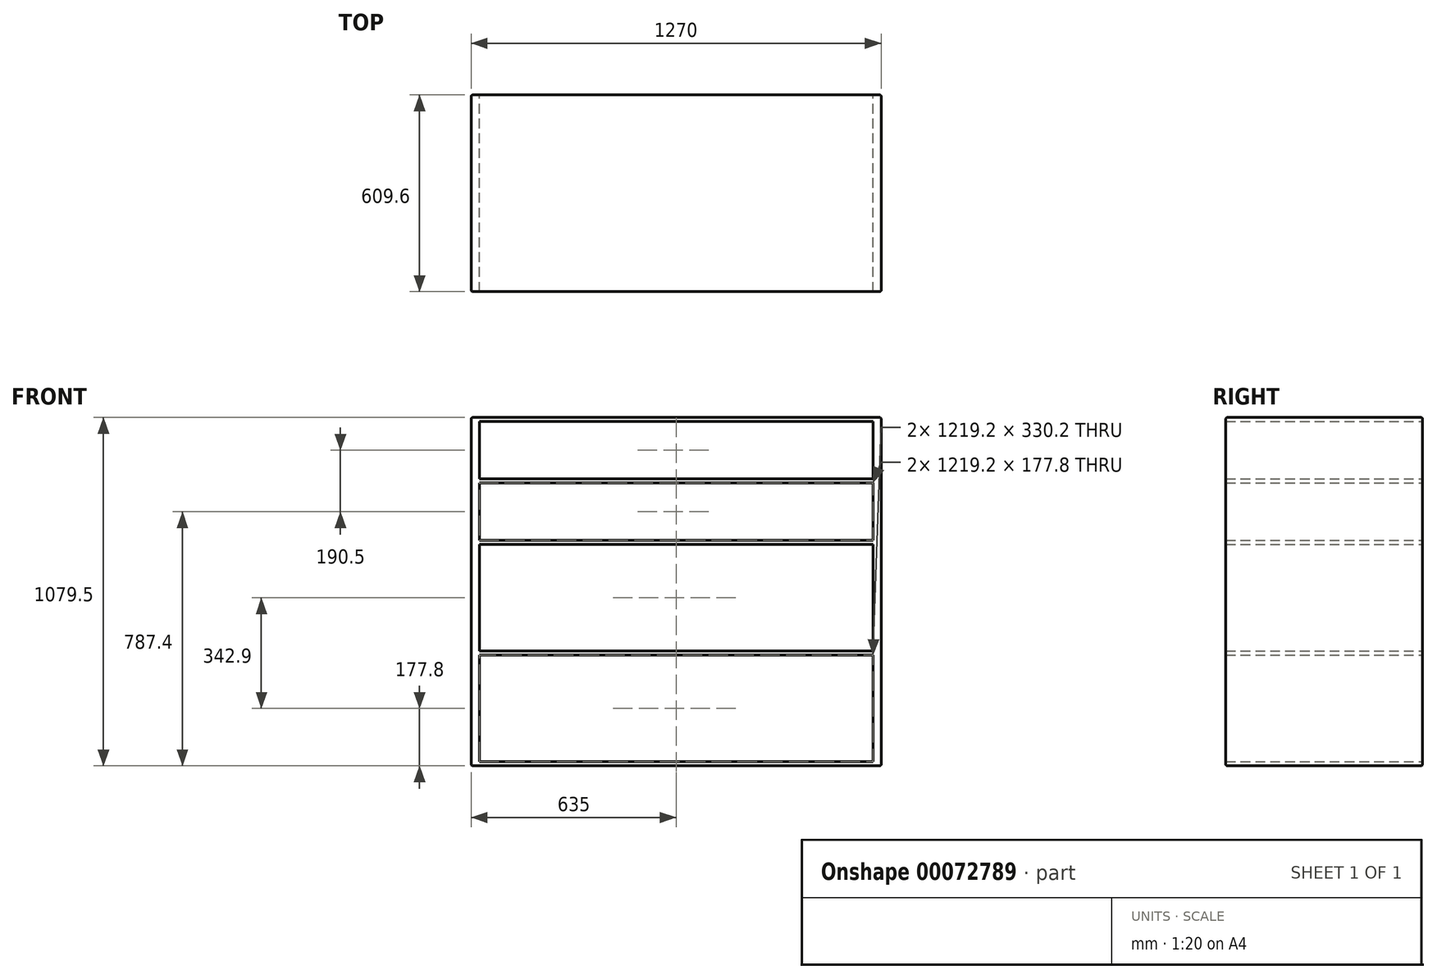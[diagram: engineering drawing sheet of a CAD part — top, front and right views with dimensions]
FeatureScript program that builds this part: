
annotation { "Feature Type Name" : "Feature", "Feature Type Description" : "" }
export const myFeature = defineFeature(function(context is Context, id is Id, definition is map)
    precondition{}
    {
        {
            var Q0;
            Q0=qCreatedBy(makeId("Right.planeOp"),FACE);
            var sketch = newSketch(context, id + "F0", { "sketchPlane" : qUnion([Q0])});
            skLineSegment(sketch, "E0.bottom", {"start": v(0, 0) * mm, "end": v(609.6, 0) * mm});
            skLineSegment(sketch, "E0.top", {"start": v(0, 1079.5) * mm, "end": v(609.6, 1079.5) * mm});
            skLineSegment(sketch, "E0.left", {"start": v(0, 0) * mm, "end": v(0, 1079.5) * mm});
            skLineSegment(sketch, "E0.right", {"start": v(609.6, 0) * mm, "end": v(609.6, 1079.5) * mm});
            skSolve(sketch);
        }
        {
            var Q0;
            Q0=makeQuery(id+"F0.imprint","IMPRINT",FACE,{"disambiguationData":[TD([[makeQuery(id+"F0.imprint","IMPRINT",EDGE,{"derivedFrom":sQuery(id+"F0.wireOp",EDGE,"E0.bottom")}),1.0]])]});
            extrude(context, id + "F1", {"entities" : qUnion([Q0]), "depth" : 25.4 * mm});
        }
        {
            var Q0;
            Q0=makeQuery(id+"F1.opExtrude","CAP_FACE",FACE,{"disambiguationData":[OSD([sQuery(id+"F0.wireOp",EDGE,"E0.bottom"),sQuery(id+"F0.wireOp",EDGE,"E0.top"),sQuery(id+"F0.wireOp",EDGE,"E0.left"),sQuery(id+"F0.wireOp",EDGE,"E0.right")])],"isStart":false});
            var sketch = newSketch(context, id + "F2", { "sketchPlane" : qUnion([Q0])});
            skLineSegment(sketch, "E1.bottom", {"start": v(0, 0) * mm, "end": v(609.6, 0) * mm});
            skLineSegment(sketch, "E1.top", {"start": v(0, 12.7) * mm, "end": v(609.6, 12.7) * mm});
            skLineSegment(sketch, "E1.left", {"start": v(0, 0) * mm, "end": v(0, 12.7) * mm});
            skLineSegment(sketch, "E1.right", {"start": v(609.6, 0) * mm, "end": v(609.6, 12.7) * mm});
            skSolve(sketch);
        }
        {
            var Q0;
            Q0=makeQuery(id+"F2.imprint","IMPRINT",FACE,{"disambiguationData":[TD([[makeQuery(id+"F2.imprint","IMPRINT",EDGE,{"derivedFrom":sQuery(id+"F2.wireOp",EDGE,"E1.bottom")}),1.0]])]});
            extrude(context, id + "F3", {"entities" : qUnion([Q0]), "operationType" : NewBodyOperationType.ADD, "depth" : 609.6 * mm});
        }
        {
            var Q0;
            Q0=makeQuery(id+"F1.opExtrude","CAP_FACE",FACE,{"disambiguationData":[OSD([sQuery(id+"F0.wireOp",EDGE,"E0.bottom"),sQuery(id+"F0.wireOp",EDGE,"E0.top"),sQuery(id+"F0.wireOp",EDGE,"E0.left"),sQuery(id+"F0.wireOp",EDGE,"E0.right")])],"isStart":false});
            var sketch = newSketch(context, id + "F4", { "sketchPlane" : qUnion([Q0])});
            skLineSegment(sketch, "E2", {"start": v(0, 12.7) * mm, "end": v(0, 342.9) * mm});
            skLineSegment(sketch, "E3.bottom", {"start": v(0, 342.9) * mm, "end": v(609.6, 342.9) * mm});
            skLineSegment(sketch, "E3.top", {"start": v(0, 355.6) * mm, "end": v(609.6, 355.6) * mm});
            skLineSegment(sketch, "E3.left", {"start": v(0, 342.9) * mm, "end": v(0, 355.6) * mm});
            skLineSegment(sketch, "E3.right", {"start": v(609.6, 342.9) * mm, "end": v(609.6, 355.6) * mm});
            skSolve(sketch);
        }
        {
            var Q0;
            Q0=makeQuery(id+"F4.imprint","IMPRINT",FACE,{"disambiguationData":[TD([[makeQuery(id+"F4.imprint","IMPRINT",EDGE,{"derivedFrom":sQuery(id+"F4.wireOp",EDGE,"E3.bottom")}),1.0]])]});
            extrude(context, id + "F5", {"entities" : qUnion([Q0]), "operationType" : NewBodyOperationType.ADD, "depth" : 609.6 * mm});
        }
        {
            var Q0;
            {var subQ0=sQuery(id+"F0.wireOp",EDGE,"E0.right");var subQ1=sQuery(id+"F0.wireOp",EDGE,"E0.left");var subQ2=sQuery(id+"F0.wireOp",EDGE,"E0.top");Q0=makeQuery(id+"F5.boolean.opBoolean","SPLIT",FACE,{"disambiguationData":[TD([makeQuery(id+"F1.opExtrude","SWEPT_FACE",FACE,{"disambiguationData":[OSD([subQ2])]})])],"derivedFrom":makeQuery(id+"F1.opExtrude","CAP_FACE",FACE,{"disambiguationData":[OSD([sQuery(id+"F0.wireOp",EDGE,"E0.bottom"),subQ2,subQ1,subQ0])],"isStart":false})});}
            var sketch = newSketch(context, id + "F6", { "sketchPlane" : qUnion([Q0])});
            skLineSegment(sketch, "E4", {"start": v(0, 355.6) * mm, "end": v(0, 685.8) * mm});
            skLineSegment(sketch, "E5.bottom", {"start": v(0, 685.8) * mm, "end": v(609.6, 685.8) * mm});
            skLineSegment(sketch, "E5.top", {"start": v(0, 698.5) * mm, "end": v(609.6, 698.5) * mm});
            skLineSegment(sketch, "E5.left", {"start": v(0, 685.8) * mm, "end": v(0, 698.5) * mm});
            skLineSegment(sketch, "E5.right", {"start": v(609.6, 685.8) * mm, "end": v(609.6, 698.5) * mm});
            skSolve(sketch);
        }
        {
            var Q0;
            Q0=makeQuery(id+"F6.imprint","IMPRINT",FACE,{"disambiguationData":[TD([[makeQuery(id+"F6.imprint","IMPRINT",EDGE,{"derivedFrom":sQuery(id+"F6.wireOp",EDGE,"E5.bottom")}),1.0]])]});
            extrude(context, id + "F7", {"entities" : qUnion([Q0]), "operationType" : NewBodyOperationType.ADD, "depth" : 609.6 * mm});
        }
        {
            var Q0;
            {var subQ1=sQuery(id+"F0.wireOp",EDGE,"E0.right");var subQ4=sQuery(id+"F0.wireOp",EDGE,"E0.left");var subQ7=sQuery(id+"F0.wireOp",EDGE,"E0.top");var subQ8=makeQuery(id+"F1.opExtrude","SWEPT_FACE",FACE,{"disambiguationData":[OSD([subQ7])]});Q0=makeQuery(id+"F7.boolean.opBoolean","SPLIT",FACE,{"disambiguationData":[TD([subQ8])],"derivedFrom":makeQuery(id+"F5.boolean.opBoolean","SPLIT",FACE,{"disambiguationData":[TD([subQ8])],"derivedFrom":makeQuery(id+"F1.opExtrude","CAP_FACE",FACE,{"disambiguationData":[OSD([sQuery(id+"F0.wireOp",EDGE,"E0.bottom"),subQ7,subQ4,subQ1])],"isStart":false})})});}
            var sketch = newSketch(context, id + "F8", { "sketchPlane" : qUnion([Q0])});
            skLineSegment(sketch, "E6", {"start": v(0, 698.5) * mm, "end": v(0, 876.3) * mm});
            skLineSegment(sketch, "E7.bottom", {"start": v(0, 876.3) * mm, "end": v(609.6, 876.3) * mm});
            skLineSegment(sketch, "E7.top", {"start": v(0, 889) * mm, "end": v(609.6, 889) * mm});
            skLineSegment(sketch, "E7.left", {"start": v(0, 876.3) * mm, "end": v(0, 889) * mm});
            skLineSegment(sketch, "E7.right", {"start": v(609.6, 876.3) * mm, "end": v(609.6, 889) * mm});
            skSolve(sketch);
        }
        {
            var Q0;
            Q0=makeQuery(id+"F8.imprint","IMPRINT",FACE,{"disambiguationData":[TD([[makeQuery(id+"F8.imprint","IMPRINT",EDGE,{"derivedFrom":sQuery(id+"F8.wireOp",EDGE,"E7.bottom")}),1.0]])]});
            extrude(context, id + "F9", {"entities" : qUnion([Q0]), "operationType" : NewBodyOperationType.ADD, "depth" : 609.6 * mm});
        }
        {
            var Q0;
            {var subQ3=sQuery(id+"F0.wireOp",EDGE,"E0.top");var subQ4=makeQuery(id+"F1.opExtrude","SWEPT_FACE",FACE,{"disambiguationData":[OSD([subQ3])]});var subQ7=sQuery(id+"F0.wireOp",EDGE,"E0.left");var subQ10=sQuery(id+"F0.wireOp",EDGE,"E0.right");Q0=makeQuery(id+"F9.boolean.opBoolean","SPLIT",FACE,{"disambiguationData":[TD([subQ4])],"derivedFrom":makeQuery(id+"F7.boolean.opBoolean","SPLIT",FACE,{"disambiguationData":[TD([subQ4])],"derivedFrom":makeQuery(id+"F5.boolean.opBoolean","SPLIT",FACE,{"disambiguationData":[TD([subQ4])],"derivedFrom":makeQuery(id+"F1.opExtrude","CAP_FACE",FACE,{"disambiguationData":[OSD([sQuery(id+"F0.wireOp",EDGE,"E0.bottom"),subQ3,subQ7,subQ10])],"isStart":false})})})});}
            var sketch = newSketch(context, id + "F10", { "sketchPlane" : qUnion([Q0])});
            skLineSegment(sketch, "E8.bottom", {"start": v(0, 1079.5) * mm, "end": v(609.6, 1079.5) * mm});
            skLineSegment(sketch, "E8.top", {"start": v(0, 1066.8) * mm, "end": v(609.6, 1066.8) * mm});
            skLineSegment(sketch, "E8.left", {"start": v(0, 1079.5) * mm, "end": v(0, 1066.8) * mm});
            skLineSegment(sketch, "E8.right", {"start": v(609.6, 1079.5) * mm, "end": v(609.6, 1066.8) * mm});
            skSolve(sketch);
        }
        {
            var Q0;
            Q0=makeQuery(id+"F10.imprint","IMPRINT",FACE,{"disambiguationData":[TD([[makeQuery(id+"F10.imprint","IMPRINT",EDGE,{"derivedFrom":sQuery(id+"F10.wireOp",EDGE,"E8.bottom")}),-1.0]])]});
            extrude(context, id + "F11", {"entities" : qUnion([Q0]), "operationType" : NewBodyOperationType.ADD, "depth" : 609.6 * mm});
        }
        {
            var Q0;
            Q0=makeQuery(id+"F1.opExtrude","SWEPT_BODY",BODY,{"disambiguationData":[OSD([sQuery(id+"F0.wireOp",EDGE,"E0.bottom"),sQuery(id+"F0.wireOp",EDGE,"E0.top"),sQuery(id+"F0.wireOp",EDGE,"E0.left"),sQuery(id+"F0.wireOp",EDGE,"E0.right")])]});
            var Q1;
            Q1=makeQuery(id+"F3.opExtrude","CAP_FACE",FACE,{"disambiguationData":[OSD([sQuery(id+"F2.wireOp",EDGE,"E1.bottom"),sQuery(id+"F2.wireOp",EDGE,"E1.top"),sQuery(id+"F2.wireOp",EDGE,"E1.left"),sQuery(id+"F2.wireOp",EDGE,"E1.right")])],"isStart":false});
            mirror(context, id + "F12", {"operationType" : NewBodyOperationType.ADD, "entities" : qUnion([Q0]), "mirrorPlane" : qUnion([Q1])});
        }
        {
            var Q0;
            Q0=makeQuery(id+"F1.opExtrude","CAP_EDGE",EDGE,{"disambiguationData":[OSD([sQuery(id+"F0.wireOp",EDGE,"E0.top")])],"isStart":true});
            fillet(context, id + "F13", {"entities" : qUnion([Q0]), "radius" : 5.08 * mm, "tangentPropagation" : true, "allowEdgeOverflow" : false});
        }
        {
            var Q0;
            Q0=makeQuery(id+"F12.opPattern","COPY",EDGE,{"derivedFrom":makeQuery(id+"F1.opExtrude","CAP_EDGE",EDGE,{"disambiguationData":[OSD([sQuery(id+"F0.wireOp",EDGE,"E0.top")])],"isStart":true}),"instanceName":"1"});
            fillet(context, id + "F14", {"entities" : qUnion([Q0]), "radius" : 5.08 * mm, "tangentPropagation" : true, "allowEdgeOverflow" : false});
        }
        {
            var Q0;
            Q0=makeQuery(id+"F12.opPattern","COPY",EDGE,{"derivedFrom":makeQuery(id+"F1.opExtrude","CAP_EDGE",EDGE,{"disambiguationData":[OSD([sQuery(id+"F0.wireOp",EDGE,"E0.bottom")])],"isStart":true}),"instanceName":"1"});
            fillet(context, id + "F15", {"entities" : qUnion([Q0]), "radius" : 5.08 * mm, "tangentPropagation" : true, "allowEdgeOverflow" : false});
        }
        {
            var Q0;
            Q0=makeQuery(id+"F1.opExtrude","CAP_EDGE",EDGE,{"disambiguationData":[OSD([sQuery(id+"F0.wireOp",EDGE,"E0.bottom")])],"isStart":true});
            fillet(context, id + "F16", {"entities" : qUnion([Q0]), "radius" : 5.08 * mm, "tangentPropagation" : true, "allowEdgeOverflow" : false});
        }
        {
            var Q0;
            {var subQ0=makeQuery(id+"F11.boolean.opBoolean","MERGE",EDGE,{"derivedFrom":[makeQuery(id+"F1.opExtrude","SWEPT_EDGE",EDGE,{"disambiguationData":[OSD([sQuery(id+"F0.wireOp",EDGE,"E0.top"),sQuery(id+"F0.wireOp",EDGE,"E0.left")])]}),makeQuery(id+"F11.opExtrude","SWEPT_EDGE",EDGE,{"disambiguationData":[OSD([sQuery(id+"F10.wireOp",EDGE,"E8.bottom"),sQuery(id+"F10.wireOp",EDGE,"E8.left")])]})]});Q0=makeQuery(id+"F12.boolean.opBoolean","MERGE",EDGE,{"derivedFrom":[subQ0,makeQuery(id+"F12.opPattern","COPY",EDGE,{"derivedFrom":subQ0,"instanceName":"1"})]});}
            fillet(context, id + "F17", {"entities" : qUnion([Q0]), "radius" : 5.08 * mm, "tangentPropagation" : true, "allowEdgeOverflow" : false});
        }
        {
            var Q0;
            {var subQ0=makeQuery(id+"F11.boolean.opBoolean","MERGE",EDGE,{"derivedFrom":[makeQuery(id+"F1.opExtrude","SWEPT_EDGE",EDGE,{"disambiguationData":[OSD([sQuery(id+"F0.wireOp",EDGE,"E0.top"),sQuery(id+"F0.wireOp",EDGE,"E0.right")])]}),makeQuery(id+"F11.opExtrude","SWEPT_EDGE",EDGE,{"disambiguationData":[OSD([sQuery(id+"F10.wireOp",EDGE,"E8.bottom"),sQuery(id+"F10.wireOp",EDGE,"E8.right")])]})]});Q0=makeQuery(id+"F12.boolean.opBoolean","MERGE",EDGE,{"derivedFrom":[subQ0,makeQuery(id+"F12.opPattern","COPY",EDGE,{"derivedFrom":subQ0,"instanceName":"1"})]});}
            fillet(context, id + "F18", {"entities" : qUnion([Q0]), "radius" : 5.08 * mm, "tangentPropagation" : true, "allowEdgeOverflow" : false});
        }
    });
